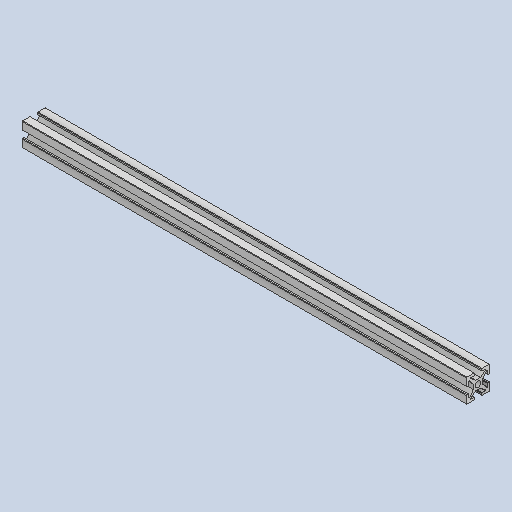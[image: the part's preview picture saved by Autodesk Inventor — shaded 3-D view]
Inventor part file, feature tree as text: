
AUTODESK INVENTOR PART (.ipt)
format: ipt  version: 2023 (Build 270158000, 158)  size: 369,664 bytes
history: native  units: mm
features: extrude x1, sketch x1
ambient origin geometry x8: Origin, YZ Plane, XZ Plane, XY Plane, X Axis, Y Axis, Z Axis, Center Point
bodies: Solide1 (feature_tree)
feature tree (2):
  extrude  "Extrusion1"  Depth=10.0mm
  sketch  "Esquisse1"
